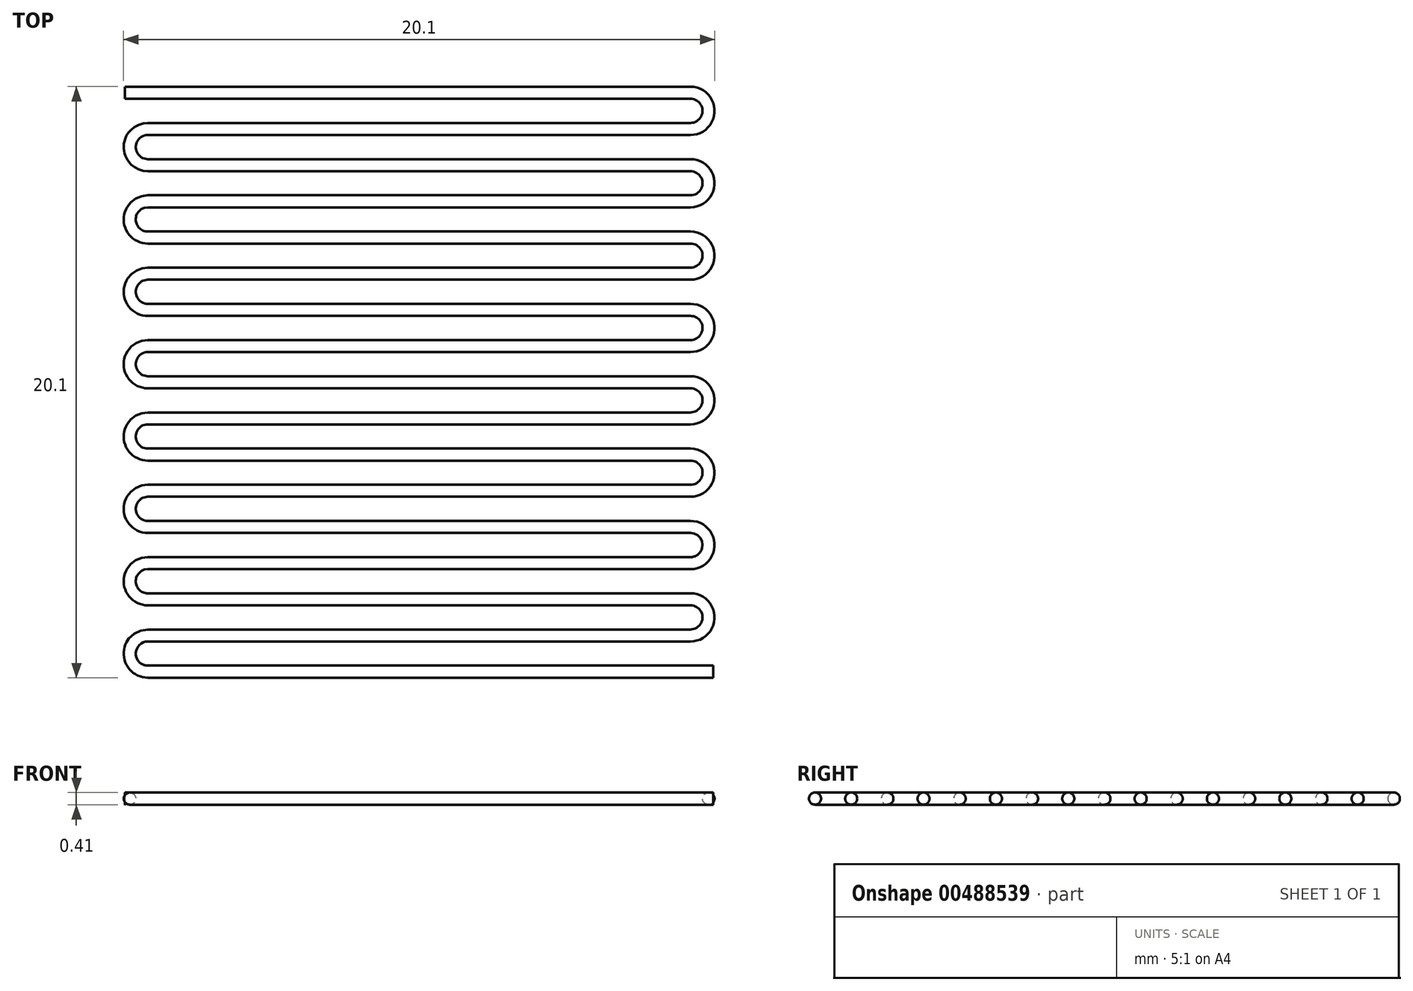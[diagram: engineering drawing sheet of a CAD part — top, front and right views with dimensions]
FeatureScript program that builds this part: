
annotation { "Feature Type Name" : "Feature", "Feature Type Description" : "" }
export const myFeature = defineFeature(function(context is Context, id is Id, definition is map)
    precondition{}
    {
        {
            assignVariable(context, id + "F0", {"name" : "d", "anyValue" : 0.4 * mm});
        }
        {
            var Q0;
            Q0=qCreatedBy(makeId("Top.planeOp"),FACE);
            cPlane(context, id + "F1", {"entities" : qUnion([Q0]), "cplaneType" : CPlaneType.OFFSET, "offset" : getVariable(context, 'd') / 2, "width" : 150 * mm, "height" : 150 * mm});
        }
        {
            var Q0;
            Q0=qCreatedBy(id+"F1.planeOp",FACE);
            var sketch = newSketch(context, id + "F2", { "sketchPlane" : qUnion([Q0])});
            skLineSegment(sketch, "E0.bottom", {"start": v(10, 10) * mm, "end": v(-10, 10) * mm});
            skLineSegment(sketch, "E0.top", {"start": v(10, -10) * mm, "end": v(-10, -10) * mm});
            skLineSegment(sketch, "E0.left", {"start": v(10, 10) * mm, "end": v(10, -10) * mm});
            skLineSegment(sketch, "E0.right", {"start": v(-10, 10) * mm, "end": v(-10, -10) * mm});
            skPoint(sketch, "E0.middle", {"position": v(0, 0) * mm});
            skLineSegment(sketch, "E1", {"start": v(-9.84, 10) * mm, "end": v(-8.61, 10) * mm});
            skLineSegment(sketch, "E2", {"start": v(-8.61, 10) * mm, "end": v(-7.38, 10) * mm});
            skLineSegment(sketch, "E3", {"start": v(-7.38, 10) * mm, "end": v(-6.15, 10) * mm});
            skLineSegment(sketch, "E4", {"start": v(-6.15, 10) * mm, "end": v(-4.92, 10) * mm});
            skLineSegment(sketch, "E5", {"start": v(-4.92, 10) * mm, "end": v(-3.7, 10) * mm});
            skLineSegment(sketch, "E6", {"start": v(-3.7, 10) * mm, "end": v(-2.46, 10) * mm});
            skLineSegment(sketch, "E7", {"start": v(-2.46, 10) * mm, "end": v(-1.23, 10) * mm});
            skLineSegment(sketch, "E8", {"start": v(-1.23, 10) * mm, "end": v(0, 10) * mm});
            skLineSegment(sketch, "E9", {"start": v(0, 10) * mm, "end": v(1.23, 10) * mm});
            skLineSegment(sketch, "E10", {"start": v(1.23, 10) * mm, "end": v(2.46, 10) * mm});
            skLineSegment(sketch, "E11", {"start": v(2.46, 10) * mm, "end": v(3.69, 10) * mm});
            skLineSegment(sketch, "E12", {"start": v(3.69, 10) * mm, "end": v(4.92, 10) * mm});
            skLineSegment(sketch, "E13", {"start": v(4.92, 10) * mm, "end": v(6.15, 10) * mm});
            skLineSegment(sketch, "E14", {"start": v(6.15, 10) * mm, "end": v(7.38, 10) * mm});
            skLineSegment(sketch, "E15", {"start": v(7.38, 10) * mm, "end": v(8.6, 10) * mm});
            skLineSegment(sketch, "E16", {"start": v(8.6, 10) * mm, "end": v(9.84, 10) * mm});
            skLineSegment(sketch, "E17", {"start": v(-9.84, 10) * mm, "end": v(-9.84, -10) * mm});
            skLineSegment(sketch, "E18", {"start": v(-8.61, 10) * mm, "end": v(-8.6, -10) * mm});
            skLineSegment(sketch, "E19", {"start": v(-8.6, -10) * mm, "end": v(-9.84, -10) * mm});
            skLineSegment(sketch, "E20", {"start": v(-7.38, 10) * mm, "end": v(-7.38, -10) * mm});
            skLineSegment(sketch, "E21", {"start": v(-7.38, -10) * mm, "end": v(-8.6, -10) * mm});
            skLineSegment(sketch, "E22", {"start": v(-6.15, 10) * mm, "end": v(-6.15, -10) * mm});
            skLineSegment(sketch, "E23", {"start": v(-6.15, -10) * mm, "end": v(-7.38, -10) * mm});
            skLineSegment(sketch, "E24", {"start": v(-4.92, 10) * mm, "end": v(-4.92, -10) * mm});
            skLineSegment(sketch, "E25", {"start": v(-4.92, -10) * mm, "end": v(-6.15, -10) * mm});
            skLineSegment(sketch, "E26", {"start": v(-3.7, 10) * mm, "end": v(-3.69, -10) * mm});
            skLineSegment(sketch, "E27", {"start": v(-3.69, -10) * mm, "end": v(-4.92, -10) * mm});
            skLineSegment(sketch, "E28", {"start": v(-2.46, 10) * mm, "end": v(-2.46, -10) * mm});
            skLineSegment(sketch, "E29", {"start": v(-2.46, -10) * mm, "end": v(-3.69, -10) * mm});
            skLineSegment(sketch, "E30", {"start": v(-1.23, 10) * mm, "end": v(-1.23, -10) * mm});
            skLineSegment(sketch, "E31", {"start": v(-1.23, -10) * mm, "end": v(-2.46, -10) * mm});
            skLineSegment(sketch, "E32", {"start": v(0, 10) * mm, "end": v(0, -10) * mm});
            skLineSegment(sketch, "E33", {"start": v(0, -10) * mm, "end": v(-1.23, -10) * mm});
            skLineSegment(sketch, "E34", {"start": v(1.23, 10) * mm, "end": v(1.23, -10) * mm});
            skLineSegment(sketch, "E35", {"start": v(1.23, -10) * mm, "end": v(0, -10) * mm});
            skLineSegment(sketch, "E36", {"start": v(2.46, 10) * mm, "end": v(2.46, -10) * mm});
            skLineSegment(sketch, "E37", {"start": v(2.46, -10) * mm, "end": v(1.23, -10) * mm});
            skLineSegment(sketch, "E38", {"start": v(3.69, 10) * mm, "end": v(3.69, -10) * mm});
            skLineSegment(sketch, "E39", {"start": v(3.69, -10) * mm, "end": v(2.46, -10) * mm});
            skLineSegment(sketch, "E40", {"start": v(4.92, 10) * mm, "end": v(4.92, -10) * mm});
            skLineSegment(sketch, "E41", {"start": v(4.92, -10) * mm, "end": v(3.69, -10) * mm});
            skLineSegment(sketch, "E42", {"start": v(6.15, 10) * mm, "end": v(6.15, -10) * mm});
            skLineSegment(sketch, "E43", {"start": v(6.15, -10) * mm, "end": v(4.92, -10) * mm});
            skLineSegment(sketch, "E44", {"start": v(7.38, 10) * mm, "end": v(7.38, -10) * mm});
            skLineSegment(sketch, "E45", {"start": v(7.38, -10) * mm, "end": v(6.15, -10) * mm});
            skLineSegment(sketch, "E46", {"start": v(8.6, 10) * mm, "end": v(8.6, -10) * mm});
            skLineSegment(sketch, "E47", {"start": v(8.6, -10) * mm, "end": v(7.38, -10) * mm});
            skLineSegment(sketch, "E48", {"start": v(9.84, 10) * mm, "end": v(9.84, -10) * mm});
            skLineSegment(sketch, "E49", {"start": v(9.84, -10) * mm, "end": v(8.6, -10) * mm});
            skLineSegment(sketch, "E50", {"start": v(-10, 10) * mm, "end": v(-10, 9.84) * mm});
            skLineSegment(sketch, "E51", {"start": v(-10, -10) * mm, "end": v(-10, -9.84) * mm});
            skLineSegment(sketch, "E52", {"start": v(-10, 9.84) * mm, "end": v(-10, 9.23) * mm});
            skLineSegment(sketch, "E53", {"start": v(-9.84, 9.23) * mm, "end": v(-8.6, 9.23) * mm});
            skLineSegment(sketch, "E54", {"start": v(-8.6, 9.23) * mm, "end": v(-7.38, 9.23) * mm});
            skLineSegment(sketch, "E55", {"start": v(-7.38, 9.23) * mm, "end": v(-6.15, 9.23) * mm});
            skLineSegment(sketch, "E56", {"start": v(-6.15, 9.23) * mm, "end": v(-4.92, 9.23) * mm});
            skLineSegment(sketch, "E57", {"start": v(-4.92, 9.23) * mm, "end": v(-3.7, 9.23) * mm});
            skLineSegment(sketch, "E58", {"start": v(-3.7, 9.23) * mm, "end": v(-2.46, 9.23) * mm});
            skLineSegment(sketch, "E59", {"start": v(-2.46, 9.23) * mm, "end": v(-1.23, 9.23) * mm});
            skLineSegment(sketch, "E60", {"start": v(-1.23, 9.23) * mm, "end": v(0, 9.23) * mm});
            skLineSegment(sketch, "E61", {"start": v(0, 9.23) * mm, "end": v(1.23, 9.23) * mm});
            skLineSegment(sketch, "E62", {"start": v(1.23, 9.23) * mm, "end": v(2.46, 9.23) * mm});
            skLineSegment(sketch, "E63", {"start": v(2.46, 9.23) * mm, "end": v(3.69, 9.23) * mm});
            skLineSegment(sketch, "E64", {"start": v(3.69, 9.23) * mm, "end": v(4.92, 9.23) * mm});
            skLineSegment(sketch, "E65", {"start": v(4.92, 9.23) * mm, "end": v(6.15, 9.23) * mm});
            skLineSegment(sketch, "E66", {"start": v(6.15, 9.23) * mm, "end": v(7.38, 9.23) * mm});
            skLineSegment(sketch, "E67", {"start": v(7.38, 9.23) * mm, "end": v(8.6, 9.23) * mm});
            skLineSegment(sketch, "E68", {"start": v(8.6, 9.23) * mm, "end": v(9.84, 9.23) * mm});
            skLineSegment(sketch, "E69", {"start": v(-10, -9.84) * mm, "end": v(-10, -9.22) * mm});
            skLineSegment(sketch, "E70", {"start": v(-9.84, -9.22) * mm, "end": v(-8.6, -9.22) * mm});
            skLineSegment(sketch, "E71", {"start": v(-8.6, -9.22) * mm, "end": v(-7.38, -9.22) * mm});
            skLineSegment(sketch, "E72", {"start": v(-7.38, -9.22) * mm, "end": v(-6.15, -9.22) * mm});
            skLineSegment(sketch, "E73", {"start": v(-6.15, -9.22) * mm, "end": v(-4.92, -9.22) * mm});
            skLineSegment(sketch, "E74", {"start": v(-4.92, -9.22) * mm, "end": v(-3.69, -9.22) * mm});
            skLineSegment(sketch, "E75", {"start": v(-3.69, -9.22) * mm, "end": v(-2.46, -9.22) * mm});
            skLineSegment(sketch, "E76", {"start": v(-2.46, -9.22) * mm, "end": v(-1.23, -9.22) * mm});
            skLineSegment(sketch, "E77", {"start": v(-1.23, -9.22) * mm, "end": v(0, -9.22) * mm});
            skLineSegment(sketch, "E78", {"start": v(0, -9.22) * mm, "end": v(1.23, -9.22) * mm});
            skLineSegment(sketch, "E79", {"start": v(1.23, -9.22) * mm, "end": v(2.46, -9.22) * mm});
            skLineSegment(sketch, "E80", {"start": v(2.46, -9.22) * mm, "end": v(3.69, -9.22) * mm});
            skLineSegment(sketch, "E81", {"start": v(3.69, -9.22) * mm, "end": v(4.92, -9.22) * mm});
            skLineSegment(sketch, "E82", {"start": v(4.92, -9.22) * mm, "end": v(6.15, -9.22) * mm});
            skLineSegment(sketch, "E83", {"start": v(6.15, -9.22) * mm, "end": v(7.38, -9.22) * mm});
            skLineSegment(sketch, "E84", {"start": v(7.38, -9.22) * mm, "end": v(8.6, -9.22) * mm});
            skLineSegment(sketch, "E85", {"start": v(8.6, -9.22) * mm, "end": v(9.84, -9.22) * mm});
            skLineSegment(sketch, "E86", {"start": v(-9.84, -9.22) * mm, "end": v(-9.84, 9.23) * mm});
            skLineSegment(sketch, "E87", {"start": v(-8.61, 9.23) * mm, "end": v(-8.6, -9.22) * mm});
            skLineSegment(sketch, "E88", {"start": v(-7.38, -9.22) * mm, "end": v(-7.38, 9.23) * mm});
            skLineSegment(sketch, "E89", {"start": v(-6.15, 9.23) * mm, "end": v(-6.15, -9.22) * mm});
            skLineSegment(sketch, "E90", {"start": v(-4.92, -9.22) * mm, "end": v(-4.92, 9.23) * mm});
            skLineSegment(sketch, "E91", {"start": v(-3.7, 9.23) * mm, "end": v(-3.69, -9.22) * mm});
            skLineSegment(sketch, "E92", {"start": v(-2.46, -9.22) * mm, "end": v(-2.46, 9.23) * mm});
            skLineSegment(sketch, "E93", {"start": v(-1.23, 9.23) * mm, "end": v(-1.23, -9.22) * mm});
            skLineSegment(sketch, "E94", {"start": v(0, -9.22) * mm, "end": v(0, 9.23) * mm});
            skLineSegment(sketch, "E95", {"start": v(1.23, 9.23) * mm, "end": v(1.23, -9.22) * mm});
            skLineSegment(sketch, "E96", {"start": v(2.46, -9.22) * mm, "end": v(2.46, 9.23) * mm});
            skLineSegment(sketch, "E97", {"start": v(3.69, 9.23) * mm, "end": v(3.69, -9.22) * mm});
            skLineSegment(sketch, "E98", {"start": v(4.92, -9.22) * mm, "end": v(4.92, 9.23) * mm});
            skLineSegment(sketch, "E99", {"start": v(6.15, -9.22) * mm, "end": v(6.15, 9.23) * mm});
            skLineSegment(sketch, "E100", {"start": v(7.38, 9.23) * mm, "end": v(7.38, -9.22) * mm});
            skLineSegment(sketch, "E101", {"start": v(8.6, -9.22) * mm, "end": v(8.6, 9.23) * mm});
            skLineSegment(sketch, "E102", {"start": v(9.84, 9.23) * mm, "end": v(9.84, -9.22) * mm});
            skArc(sketch, "E103", {"start": v(9.84, 9.23) * mm, "mid": v(9.22, 9.84) * mm, "end": v(8.6, 9.23) * mm});
            skArc(sketch, "E104", {"start": v(7.38, 9.23) * mm, "mid": v(6.76, 9.84) * mm, "end": v(6.15, 9.23) * mm});
            skArc(sketch, "E105", {"start": v(4.92, 9.23) * mm, "mid": v(4.3, 9.84) * mm, "end": v(3.69, 9.23) * mm});
            skArc(sketch, "E106", {"start": v(2.46, 9.23) * mm, "mid": v(1.84, 9.84) * mm, "end": v(1.23, 9.23) * mm});
            skArc(sketch, "E107", {"start": v(0, 9.23) * mm, "mid": v(-0.62, 9.84) * mm, "end": v(-1.23, 9.23) * mm});
            skArc(sketch, "E108", {"start": v(-2.46, 9.23) * mm, "mid": v(-3.07, 9.84) * mm, "end": v(-3.69, 9.23) * mm});
            skArc(sketch, "E109", {"start": v(-4.92, 9.23) * mm, "mid": v(-5.54, 9.84) * mm, "end": v(-6.15, 9.23) * mm});
            skArc(sketch, "E110", {"start": v(-7.38, 9.23) * mm, "mid": v(-8, 9.84) * mm, "end": v(-8.6, 9.23) * mm});
            skArc(sketch, "E111", {"start": v(4.92, -9.22) * mm, "mid": v(5.53, -9.84) * mm, "end": v(6.15, -9.22) * mm});
            skArc(sketch, "E112", {"start": v(2.46, -9.22) * mm, "mid": v(3.07, -9.84) * mm, "end": v(3.69, -9.22) * mm});
            skArc(sketch, "E113", {"start": v(0, -9.22) * mm, "mid": v(0.62, -9.84) * mm, "end": v(1.23, -9.22) * mm});
            skArc(sketch, "E114", {"start": v(-2.46, -9.22) * mm, "mid": v(-1.85, -9.84) * mm, "end": v(-1.23, -9.22) * mm});
            skArc(sketch, "E115", {"start": v(-4.92, -9.22) * mm, "mid": v(-4.3, -9.84) * mm, "end": v(-3.69, -9.22) * mm});
            skArc(sketch, "E116", {"start": v(-9.84, -9.22) * mm, "mid": v(-9.22, -9.84) * mm, "end": v(-8.6, -9.22) * mm});
            skArc(sketch, "E117", {"start": v(7.38, -9.22) * mm, "mid": v(8, -9.84) * mm, "end": v(8.6, -9.22) * mm});
            skArc(sketch, "E118", {"start": v(-7.38, -9.22) * mm, "mid": v(-6.77, -9.84) * mm, "end": v(-6.15, -9.22) * mm});
            skLineSegment(sketch, "E119", {"start": v(-10, 10) * mm, "end": v(-9.84, 10) * mm});
            skLineSegment(sketch, "E120", {"start": v(9.84, 10) * mm, "end": v(10, 10) * mm});
            skLineSegment(sketch, "E121", {"start": v(-10, 9.84) * mm, "end": v(10, 9.84) * mm});
            skLineSegment(sketch, "E122", {"start": v(-10, -9.84) * mm, "end": v(10, -9.84) * mm});
            skLineSegment(sketch, "E123", {"start": v(9.84, -10) * mm, "end": v(9.84, 9.23) * mm});
            skLineSegment(sketch, "E124", {"start": v(-9.84, -9.22) * mm, "end": v(-9.84, 10) * mm});
            skSolve(sketch);
        }
        {
            var Q0;
            Q0=sQuery(id+"F2.wireOp",EDGE,"E123");
            var Q1;
            Q1=sQuery(id+"F2.wireOp",VERTEX,"E123.start");
            cPlane(context, id + "F3", {"entities" : qUnion([Q0, Q1]), "cplaneType" : CPlaneType.LINE_POINT, "offset" : 25 * mm, "width" : 150 * mm, "height" : 150 * mm});
        }
        {
            var Q0;
            Q0=qCreatedBy(id+"F3.planeOp",FACE);
            var sketch = newSketch(context, id + "F4", { "sketchPlane" : qUnion([Q0])});
            skCircle(sketch, "E125", {"center": v(-9.84, 0.2) * mm, "radius": 0.2 * mm});
            skSolve(sketch);
        }
        {
            var Q0;
            Q0=qCreatedBy(id+"F1.planeOp",FACE);
            cPlane(context, id + "F5", {"entities" : qUnion([Q0]), "cplaneType" : CPlaneType.OFFSET, "offset" : getVariable(context, 'd'), "width" : 150 * mm, "height" : 150 * mm});
        }
        {
            var Q0;
            Q0=qCreatedBy(id+"F5.planeOp",FACE);
            var sketch = newSketch(context, id + "F6", { "sketchPlane" : qUnion([Q0])});
            skLineSegment(sketch, "E126.bottom", {"start": v(-30, 10) * mm, "end": v(-30, -10) * mm});
            skLineSegment(sketch, "E126.top", {"start": v(-10, 10) * mm, "end": v(-10, -10) * mm});
            skLineSegment(sketch, "E126.left", {"start": v(-30, 10) * mm, "end": v(-10, 10) * mm});
            skLineSegment(sketch, "E126.right", {"start": v(-30, -10) * mm, "end": v(-10, -10) * mm});
            skPoint(sketch, "E126.middle", {"position": v(-20, 0) * mm});
            skLineSegment(sketch, "E127", {"start": v(-30, -9.84) * mm, "end": v(-30, -8.6) * mm});
            skLineSegment(sketch, "E128", {"start": v(-30, -8.6) * mm, "end": v(-30, -7.38) * mm});
            skLineSegment(sketch, "E129", {"start": v(-30, -7.38) * mm, "end": v(-30, -6.15) * mm});
            skLineSegment(sketch, "E130", {"start": v(-30, -6.15) * mm, "end": v(-30, -4.92) * mm});
            skLineSegment(sketch, "E131", {"start": v(-30, -4.92) * mm, "end": v(-30, -3.69) * mm});
            skLineSegment(sketch, "E132", {"start": v(-30, -3.69) * mm, "end": v(-30, -2.46) * mm});
            skLineSegment(sketch, "E133", {"start": v(-30, -2.46) * mm, "end": v(-30, -1.23) * mm});
            skLineSegment(sketch, "E134", {"start": v(-30, -1.23) * mm, "end": v(-30, 0) * mm});
            skLineSegment(sketch, "E135", {"start": v(-30, 0) * mm, "end": v(-30, 1.23) * mm});
            skLineSegment(sketch, "E136", {"start": v(-30, 1.23) * mm, "end": v(-30, 2.46) * mm});
            skLineSegment(sketch, "E137", {"start": v(-30, 2.46) * mm, "end": v(-30, 3.69) * mm});
            skLineSegment(sketch, "E138", {"start": v(-30, 3.69) * mm, "end": v(-30, 4.92) * mm});
            skLineSegment(sketch, "E139", {"start": v(-30, 4.92) * mm, "end": v(-30, 6.15) * mm});
            skLineSegment(sketch, "E140", {"start": v(-30, 6.15) * mm, "end": v(-30, 7.38) * mm});
            skLineSegment(sketch, "E141", {"start": v(-30, 7.38) * mm, "end": v(-30, 8.6) * mm});
            skLineSegment(sketch, "E142", {"start": v(-30, 8.6) * mm, "end": v(-30, 9.84) * mm});
            skLineSegment(sketch, "E143", {"start": v(-30, -9.84) * mm, "end": v(-10, -9.84) * mm});
            skLineSegment(sketch, "E144", {"start": v(-30, -8.6) * mm, "end": v(-10, -8.6) * mm});
            skLineSegment(sketch, "E145", {"start": v(-10, -8.6) * mm, "end": v(-10, -9.84) * mm});
            skLineSegment(sketch, "E146", {"start": v(-30, -7.38) * mm, "end": v(-10, -7.38) * mm});
            skLineSegment(sketch, "E147", {"start": v(-10, -7.38) * mm, "end": v(-10, -8.6) * mm});
            skLineSegment(sketch, "E148", {"start": v(-30, -6.15) * mm, "end": v(-10, -6.15) * mm});
            skLineSegment(sketch, "E149", {"start": v(-10, -6.15) * mm, "end": v(-10, -7.38) * mm});
            skLineSegment(sketch, "E150", {"start": v(-30, -4.92) * mm, "end": v(-10, -4.92) * mm});
            skLineSegment(sketch, "E151", {"start": v(-10, -4.92) * mm, "end": v(-10, -6.15) * mm});
            skLineSegment(sketch, "E152", {"start": v(-30, -3.69) * mm, "end": v(-10, -3.69) * mm});
            skLineSegment(sketch, "E153", {"start": v(-10, -3.69) * mm, "end": v(-10, -4.92) * mm});
            skLineSegment(sketch, "E154", {"start": v(-30, -2.46) * mm, "end": v(-10, -2.46) * mm});
            skLineSegment(sketch, "E155", {"start": v(-10, -2.46) * mm, "end": v(-10, -3.69) * mm});
            skLineSegment(sketch, "E156", {"start": v(-30, -1.23) * mm, "end": v(-10, -1.23) * mm});
            skLineSegment(sketch, "E157", {"start": v(-10, -1.23) * mm, "end": v(-10, -2.46) * mm});
            skLineSegment(sketch, "E158", {"start": v(-30, 0) * mm, "end": v(-10, 0) * mm});
            skLineSegment(sketch, "E159", {"start": v(-10, 0) * mm, "end": v(-10, -1.23) * mm});
            skLineSegment(sketch, "E160", {"start": v(-30, 1.23) * mm, "end": v(-10, 1.23) * mm});
            skLineSegment(sketch, "E161", {"start": v(-10, 1.23) * mm, "end": v(-10, 0) * mm});
            skLineSegment(sketch, "E162", {"start": v(-30, 2.46) * mm, "end": v(-10, 2.46) * mm});
            skLineSegment(sketch, "E163", {"start": v(-10, 2.46) * mm, "end": v(-10, 1.23) * mm});
            skLineSegment(sketch, "E164", {"start": v(-30, 3.7) * mm, "end": v(-10, 3.7) * mm});
            skLineSegment(sketch, "E165", {"start": v(-10, 3.7) * mm, "end": v(-10, 2.46) * mm});
            skLineSegment(sketch, "E166", {"start": v(-30, 4.92) * mm, "end": v(-10, 4.92) * mm});
            skLineSegment(sketch, "E167", {"start": v(-10, 4.92) * mm, "end": v(-10, 3.7) * mm});
            skLineSegment(sketch, "E168", {"start": v(-30, 6.15) * mm, "end": v(-10, 6.15) * mm});
            skLineSegment(sketch, "E169", {"start": v(-10, 6.15) * mm, "end": v(-10, 4.92) * mm});
            skLineSegment(sketch, "E170", {"start": v(-30, 7.38) * mm, "end": v(-10, 7.38) * mm});
            skLineSegment(sketch, "E171", {"start": v(-10, 7.38) * mm, "end": v(-10, 6.15) * mm});
            skLineSegment(sketch, "E172", {"start": v(-30, 8.6) * mm, "end": v(-10, 8.6) * mm});
            skLineSegment(sketch, "E173", {"start": v(-10, 8.6) * mm, "end": v(-10, 7.38) * mm});
            skLineSegment(sketch, "E174", {"start": v(-30, 9.84) * mm, "end": v(-10, 9.84) * mm});
            skLineSegment(sketch, "E175", {"start": v(-10, 9.84) * mm, "end": v(-10, 8.6) * mm});
            skLineSegment(sketch, "E176", {"start": v(-30, -10) * mm, "end": v(-29.84, -10) * mm});
            skLineSegment(sketch, "E177", {"start": v(-10, -10) * mm, "end": v(-10.16, -10) * mm});
            skLineSegment(sketch, "E178", {"start": v(-29.84, -10) * mm, "end": v(-29.23, -10) * mm});
            skLineSegment(sketch, "E179", {"start": v(-29.23, -9.84) * mm, "end": v(-29.23, -8.6) * mm});
            skLineSegment(sketch, "E180", {"start": v(-29.23, -8.6) * mm, "end": v(-29.23, -7.38) * mm});
            skLineSegment(sketch, "E181", {"start": v(-29.23, -7.38) * mm, "end": v(-29.23, -6.15) * mm});
            skLineSegment(sketch, "E182", {"start": v(-29.23, -6.15) * mm, "end": v(-29.23, -4.92) * mm});
            skLineSegment(sketch, "E183", {"start": v(-29.23, -4.92) * mm, "end": v(-29.23, -3.69) * mm});
            skLineSegment(sketch, "E184", {"start": v(-29.23, -3.69) * mm, "end": v(-29.23, -2.46) * mm});
            skLineSegment(sketch, "E185", {"start": v(-29.23, -2.46) * mm, "end": v(-29.23, -1.23) * mm});
            skLineSegment(sketch, "E186", {"start": v(-29.23, -1.23) * mm, "end": v(-29.23, 0) * mm});
            skLineSegment(sketch, "E187", {"start": v(-29.23, 0) * mm, "end": v(-29.23, 1.23) * mm});
            skLineSegment(sketch, "E188", {"start": v(-29.23, 1.23) * mm, "end": v(-29.23, 2.46) * mm});
            skLineSegment(sketch, "E189", {"start": v(-29.23, 2.46) * mm, "end": v(-29.23, 3.69) * mm});
            skLineSegment(sketch, "E190", {"start": v(-29.23, 3.69) * mm, "end": v(-29.23, 4.92) * mm});
            skLineSegment(sketch, "E191", {"start": v(-29.23, 4.92) * mm, "end": v(-29.23, 6.15) * mm});
            skLineSegment(sketch, "E192", {"start": v(-29.23, 6.15) * mm, "end": v(-29.23, 7.38) * mm});
            skLineSegment(sketch, "E193", {"start": v(-29.23, 7.38) * mm, "end": v(-29.23, 8.6) * mm});
            skLineSegment(sketch, "E194", {"start": v(-29.23, 8.6) * mm, "end": v(-29.23, 9.84) * mm});
            skLineSegment(sketch, "E195", {"start": v(-10.16, -10) * mm, "end": v(-10.78, -10) * mm});
            skLineSegment(sketch, "E196", {"start": v(-10.78, -9.84) * mm, "end": v(-10.78, -8.6) * mm});
            skLineSegment(sketch, "E197", {"start": v(-10.78, -8.6) * mm, "end": v(-10.78, -7.38) * mm});
            skLineSegment(sketch, "E198", {"start": v(-10.78, -7.38) * mm, "end": v(-10.78, -6.15) * mm});
            skLineSegment(sketch, "E199", {"start": v(-10.78, -6.15) * mm, "end": v(-10.78, -4.92) * mm});
            skLineSegment(sketch, "E200", {"start": v(-10.78, -4.92) * mm, "end": v(-10.78, -3.69) * mm});
            skLineSegment(sketch, "E201", {"start": v(-10.78, -3.69) * mm, "end": v(-10.78, -2.46) * mm});
            skLineSegment(sketch, "E202", {"start": v(-10.78, -2.46) * mm, "end": v(-10.78, -1.23) * mm});
            skLineSegment(sketch, "E203", {"start": v(-10.78, -1.23) * mm, "end": v(-10.78, 0) * mm});
            skLineSegment(sketch, "E204", {"start": v(-10.78, 0) * mm, "end": v(-10.78, 1.23) * mm});
            skLineSegment(sketch, "E205", {"start": v(-10.78, 1.23) * mm, "end": v(-10.78, 2.46) * mm});
            skLineSegment(sketch, "E206", {"start": v(-10.78, 2.46) * mm, "end": v(-10.78, 3.7) * mm});
            skLineSegment(sketch, "E207", {"start": v(-10.78, 3.7) * mm, "end": v(-10.78, 4.92) * mm});
            skLineSegment(sketch, "E208", {"start": v(-10.78, 4.92) * mm, "end": v(-10.78, 6.15) * mm});
            skLineSegment(sketch, "E209", {"start": v(-10.78, 6.15) * mm, "end": v(-10.78, 7.38) * mm});
            skLineSegment(sketch, "E210", {"start": v(-10.78, 7.38) * mm, "end": v(-10.78, 8.6) * mm});
            skLineSegment(sketch, "E211", {"start": v(-10.78, 8.6) * mm, "end": v(-10.78, 9.84) * mm});
            skLineSegment(sketch, "E212", {"start": v(-10.78, -9.84) * mm, "end": v(-29.23, -9.84) * mm});
            skLineSegment(sketch, "E213", {"start": v(-29.23, -8.6) * mm, "end": v(-10.78, -8.6) * mm});
            skLineSegment(sketch, "E214", {"start": v(-10.78, -7.38) * mm, "end": v(-29.23, -7.38) * mm});
            skLineSegment(sketch, "E215", {"start": v(-29.23, -6.15) * mm, "end": v(-10.78, -6.15) * mm});
            skLineSegment(sketch, "E216", {"start": v(-10.78, -4.92) * mm, "end": v(-29.23, -4.92) * mm});
            skLineSegment(sketch, "E217", {"start": v(-29.23, -3.69) * mm, "end": v(-10.78, -3.69) * mm});
            skLineSegment(sketch, "E218", {"start": v(-10.78, -2.46) * mm, "end": v(-29.23, -2.46) * mm});
            skLineSegment(sketch, "E219", {"start": v(-29.23, -1.23) * mm, "end": v(-10.78, -1.23) * mm});
            skLineSegment(sketch, "E220", {"start": v(-10.78, 0) * mm, "end": v(-29.23, 0) * mm});
            skLineSegment(sketch, "E221", {"start": v(-29.23, 1.23) * mm, "end": v(-10.78, 1.23) * mm});
            skLineSegment(sketch, "E222", {"start": v(-10.78, 2.46) * mm, "end": v(-29.23, 2.46) * mm});
            skLineSegment(sketch, "E223", {"start": v(-29.23, 3.7) * mm, "end": v(-10.78, 3.7) * mm});
            skLineSegment(sketch, "E224", {"start": v(-10.78, 4.92) * mm, "end": v(-29.23, 4.92) * mm});
            skLineSegment(sketch, "E225", {"start": v(-10.78, 6.15) * mm, "end": v(-29.23, 6.15) * mm});
            skLineSegment(sketch, "E226", {"start": v(-29.23, 7.38) * mm, "end": v(-10.78, 7.38) * mm});
            skLineSegment(sketch, "E227", {"start": v(-10.78, 8.6) * mm, "end": v(-29.23, 8.6) * mm});
            skLineSegment(sketch, "E228", {"start": v(-29.23, 9.84) * mm, "end": v(-10.78, 9.84) * mm});
            skArc(sketch, "E229", {"start": v(-29.23, 9.84) * mm, "mid": v(-29.84, 9.22) * mm, "end": v(-29.23, 8.6) * mm});
            skArc(sketch, "E230", {"start": v(-29.23, 7.38) * mm, "mid": v(-29.84, 6.76) * mm, "end": v(-29.23, 6.15) * mm});
            skArc(sketch, "E231", {"start": v(-29.23, 4.92) * mm, "mid": v(-29.84, 4.3) * mm, "end": v(-29.23, 3.69) * mm});
            skArc(sketch, "E232", {"start": v(-29.23, 2.46) * mm, "mid": v(-29.84, 1.84) * mm, "end": v(-29.23, 1.23) * mm});
            skArc(sketch, "E233", {"start": v(-29.23, 0) * mm, "mid": v(-29.84, -0.61) * mm, "end": v(-29.23, -1.23) * mm});
            skArc(sketch, "E234", {"start": v(-29.23, -2.46) * mm, "mid": v(-29.84, -3.07) * mm, "end": v(-29.23, -3.69) * mm});
            skArc(sketch, "E235", {"start": v(-29.23, -4.92) * mm, "mid": v(-29.84, -5.53) * mm, "end": v(-29.23, -6.15) * mm});
            skArc(sketch, "E236", {"start": v(-29.23, -7.38) * mm, "mid": v(-29.84, -8) * mm, "end": v(-29.23, -8.6) * mm});
            skArc(sketch, "E237", {"start": v(-10.78, 4.92) * mm, "mid": v(-10.16, 5.53) * mm, "end": v(-10.78, 6.15) * mm});
            skArc(sketch, "E238", {"start": v(-10.78, 2.46) * mm, "mid": v(-10.16, 3.08) * mm, "end": v(-10.78, 3.7) * mm});
            skArc(sketch, "E239", {"start": v(-10.78, 0) * mm, "mid": v(-10.16, 0.62) * mm, "end": v(-10.78, 1.23) * mm});
            skArc(sketch, "E240", {"start": v(-10.78, -2.46) * mm, "mid": v(-10.16, -1.84) * mm, "end": v(-10.78, -1.23) * mm});
            skArc(sketch, "E241", {"start": v(-10.78, -4.92) * mm, "mid": v(-10.16, -4.3) * mm, "end": v(-10.78, -3.69) * mm});
            skArc(sketch, "E242", {"start": v(-10.78, -9.84) * mm, "mid": v(-10.16, -9.22) * mm, "end": v(-10.78, -8.6) * mm});
            skArc(sketch, "E243", {"start": v(-10.78, 7.38) * mm, "mid": v(-10.16, 8) * mm, "end": v(-10.78, 8.6) * mm});
            skArc(sketch, "E244", {"start": v(-10.78, -7.38) * mm, "mid": v(-10.16, -6.76) * mm, "end": v(-10.78, -6.15) * mm});
            skLineSegment(sketch, "E245", {"start": v(-30, -10) * mm, "end": v(-30, -9.84) * mm});
            skLineSegment(sketch, "E246", {"start": v(-30, 9.84) * mm, "end": v(-30, 10) * mm});
            skLineSegment(sketch, "E247", {"start": v(-29.84, -10) * mm, "end": v(-29.84, 10) * mm});
            skLineSegment(sketch, "E248", {"start": v(-10.16, -10) * mm, "end": v(-10.16, 10) * mm});
            skLineSegment(sketch, "E249", {"start": v(-10, 9.84) * mm, "end": v(-29.23, 9.84) * mm});
            skLineSegment(sketch, "E250.MirrorCS", {"start": v(-10, -10) * mm, "end": v(-9.84, -10) * mm});
            skLineSegment(sketch, "E251.MirrorCS", {"start": v(10, -10) * mm, "end": v(9.84, -10) * mm});
            skLineSegment(sketch, "E252.MirrorCS", {"start": v(10, -10) * mm, "end": v(10, -9.84) * mm});
            skLineSegment(sketch, "E253.MirrorCS", {"start": v(-9.84, -10) * mm, "end": v(-9.22, -10) * mm});
            skLineSegment(sketch, "E254.MirrorCS", {"start": v(10, 9.84) * mm, "end": v(10, 10) * mm});
            skLineSegment(sketch, "E255.MirrorCS", {"start": v(9.84, -10) * mm, "end": v(9.23, -10) * mm});
            skLineSegment(sketch, "E256.MirrorCS", {"start": v(9.23, -1.23) * mm, "end": v(9.23, 0) * mm});
            skLineSegment(sketch, "E257.MirrorCS", {"start": v(-9.22, 7.38) * mm, "end": v(-9.22, 8.6) * mm});
            skLineSegment(sketch, "E258.MirrorCS", {"start": v(9.23, 9.84) * mm, "end": v(-9.22, 9.84) * mm});
            skLineSegment(sketch, "E259.MirrorCS", {"start": v(-9.22, 0) * mm, "end": v(-9.22, 1.23) * mm});
            skLineSegment(sketch, "E260.MirrorCS", {"start": v(-9.22, 0) * mm, "end": v(9.23, 0) * mm});
            skLineSegment(sketch, "E261.MirrorCS", {"start": v(10, 7.38) * mm, "end": v(10, 8.6) * mm});
            skLineSegment(sketch, "E262.MirrorCS", {"start": v(9.23, 1.23) * mm, "end": v(-9.22, 1.23) * mm});
            skLineSegment(sketch, "E263.MirrorCS", {"start": v(9.23, -8.6) * mm, "end": v(9.23, -7.38) * mm});
            skLineSegment(sketch, "E264.MirrorCS", {"start": v(-9.22, -9.84) * mm, "end": v(-9.22, -8.6) * mm});
            skLineSegment(sketch, "E265.MirrorCS", {"start": v(10, 2.46) * mm, "end": v(10, 3.69) * mm});
            skLineSegment(sketch, "E266.MirrorCS", {"start": v(10, 6.15) * mm, "end": v(10, 7.38) * mm});
            skLineSegment(sketch, "E267.MirrorCS", {"start": v(9.23, 8.6) * mm, "end": v(9.22, 9.84) * mm});
            skLineSegment(sketch, "E268.MirrorCS", {"start": v(-9.22, 4.92) * mm, "end": v(9.23, 4.92) * mm});
            skLineSegment(sketch, "E269.MirrorCS", {"start": v(-9.22, 4.92) * mm, "end": v(-9.22, 6.15) * mm});
            skLineSegment(sketch, "E270.MirrorCS", {"start": v(9.23, 6.15) * mm, "end": v(9.23, 7.38) * mm});
            skLineSegment(sketch, "E271.MirrorCS", {"start": v(10, -8.6) * mm, "end": v(-10, -8.6) * mm});
            skLineSegment(sketch, "E272.MirrorCS", {"start": v(9.23, -6.15) * mm, "end": v(9.23, -4.92) * mm});
            skLineSegment(sketch, "E273.MirrorCS", {"start": v(10, -6.15) * mm, "end": v(-10, -6.15) * mm});
            skLineSegment(sketch, "E274.MirrorCS", {"start": v(10, 9.84) * mm, "end": v(-10, 9.84) * mm});
            skLineSegment(sketch, "E275.MirrorCS", {"start": v(-9.22, 6.15) * mm, "end": v(9.23, 6.15) * mm});
            skLineSegment(sketch, "E276.MirrorCS", {"start": v(9.23, -1.23) * mm, "end": v(-9.22, -1.23) * mm});
            skLineSegment(sketch, "E277.MirrorCS", {"start": v(10, 4.92) * mm, "end": v(10, 6.15) * mm});
            skLineSegment(sketch, "E278.MirrorCS", {"start": v(-9.22, -2.46) * mm, "end": v(-9.22, -1.23) * mm});
            skLineSegment(sketch, "E279.MirrorCS", {"start": v(10, 1.23) * mm, "end": v(10, 2.46) * mm});
            skLineSegment(sketch, "E280.MirrorCS", {"start": v(9.23, -3.69) * mm, "end": v(9.23, -2.46) * mm});
            skLineSegment(sketch, "E281.MirrorCS", {"start": v(-9.22, -4.92) * mm, "end": v(-9.22, -3.69) * mm});
            skLineSegment(sketch, "E282.MirrorCS", {"start": v(10, -9.84) * mm, "end": v(-10, -9.84) * mm});
            skLineSegment(sketch, "E283.MirrorCS", {"start": v(9.23, 3.69) * mm, "end": v(9.23, 4.92) * mm});
            skLineSegment(sketch, "E284.MirrorCS", {"start": v(10, 3.69) * mm, "end": v(10, 4.92) * mm});
            skLineSegment(sketch, "E285.MirrorCS", {"start": v(9.23, 1.23) * mm, "end": v(9.23, 2.46) * mm});
            skLineSegment(sketch, "E286.MirrorCS", {"start": v(9.23, 3.7) * mm, "end": v(-9.22, 3.7) * mm});
            skLineSegment(sketch, "E287.MirrorCS", {"start": v(-9.22, 2.46) * mm, "end": v(9.22, 2.46) * mm});
            skLineSegment(sketch, "E288.MirrorCS", {"start": v(-9.22, 2.46) * mm, "end": v(-9.22, 3.7) * mm});
            skLineSegment(sketch, "E289.MirrorCS", {"start": v(10, 8.6) * mm, "end": v(10, 9.84) * mm});
            skLineSegment(sketch, "E290.MirrorCS", {"start": v(-9.22, -7.38) * mm, "end": v(-9.22, -6.15) * mm});
            skLineSegment(sketch, "E291.MirrorCS", {"start": v(10, -4.92) * mm, "end": v(-10, -4.92) * mm});
            skArc(sketch, "E292.MirrorCS", {"start": v(-9.22, -7.38) * mm, "mid": v(-9.84, -6.76) * mm, "end": v(-9.22, -6.15) * mm});
            skArc(sketch, "E293.MirrorCS", {"start": v(9.23, -7.38) * mm, "mid": v(9.84, -8) * mm, "end": v(9.23, -8.6) * mm});
            skLineSegment(sketch, "E294.MirrorCS", {"start": v(9.23, 2.46) * mm, "end": v(9.23, 3.69) * mm});
            skLineSegment(sketch, "E295.MirrorCS", {"start": v(-10, 9.84) * mm, "end": v(9.22, 9.84) * mm});
            skLineSegment(sketch, "E296.MirrorCS", {"start": v(10, 0) * mm, "end": v(10, 1.23) * mm});
            skLineSegment(sketch, "E297.MirrorCS", {"start": v(9.23, -3.69) * mm, "end": v(-9.22, -3.69) * mm});
            skArc(sketch, "E298.MirrorCS", {"start": v(9.23, 0) * mm, "mid": v(9.84, -0.61) * mm, "end": v(9.23, -1.23) * mm});
            skLineSegment(sketch, "E299.MirrorCS", {"start": v(9.23, -7.38) * mm, "end": v(9.23, -6.15) * mm});
            skLineSegment(sketch, "E300.MirrorCS", {"start": v(-9.22, -8.6) * mm, "end": v(-9.22, -7.38) * mm});
            skArc(sketch, "E301.MirrorCS", {"start": v(9.23, 4.92) * mm, "mid": v(9.84, 4.3) * mm, "end": v(9.23, 3.69) * mm});
            skLineSegment(sketch, "E302.MirrorCS", {"start": v(10, 3.7) * mm, "end": v(-10, 3.7) * mm});
            skArc(sketch, "E303.MirrorCS", {"start": v(-9.22, 4.92) * mm, "mid": v(-9.84, 5.53) * mm, "end": v(-9.22, 6.15) * mm});
            skLineSegment(sketch, "E304.MirrorCS", {"start": v(-9.22, 1.23) * mm, "end": v(-9.22, 2.46) * mm});
            skLineSegment(sketch, "E305.MirrorCS", {"start": v(10, -1.23) * mm, "end": v(10, 0) * mm});
            skLineSegment(sketch, "E306.MirrorCS", {"start": v(9.23, -9.84) * mm, "end": v(9.23, -8.6) * mm});
            skLineSegment(sketch, "E307.MirrorCS", {"start": v(10, -1.23) * mm, "end": v(-10, -1.23) * mm});
            skLineSegment(sketch, "E308.MirrorCS", {"start": v(9.23, -6.15) * mm, "end": v(-9.23, -6.15) * mm});
            skLineSegment(sketch, "E309.MirrorCS", {"start": v(-9.22, -3.69) * mm, "end": v(-9.22, -2.46) * mm});
            skLineSegment(sketch, "E310.MirrorCS", {"start": v(-9.22, -6.15) * mm, "end": v(-9.22, -4.92) * mm});
            skLineSegment(sketch, "E311.MirrorCS", {"start": v(9.84, -10) * mm, "end": v(9.84, 10) * mm});
            skLineSegment(sketch, "E312.MirrorCS", {"start": v(-9.22, -9.84) * mm, "end": v(9.22, -9.84) * mm});
            skArc(sketch, "E313.MirrorCS", {"start": v(-9.22, 2.46) * mm, "mid": v(-9.84, 3.08) * mm, "end": v(-9.22, 3.7) * mm});
            skArc(sketch, "E314.MirrorCS", {"start": v(-9.22, -4.92) * mm, "mid": v(-9.84, -4.3) * mm, "end": v(-9.22, -3.69) * mm});
            skLineSegment(sketch, "E315.MirrorCS", {"start": v(9.23, 7.38) * mm, "end": v(9.23, 8.6) * mm});
            skLineSegment(sketch, "E316.MirrorCS", {"start": v(9.23, -4.92) * mm, "end": v(9.23, -3.69) * mm});
            skLineSegment(sketch, "E317.MirrorCS", {"start": v(-9.22, 6.15) * mm, "end": v(-9.22, 7.38) * mm});
            skLineSegment(sketch, "E318.MirrorCS", {"start": v(-9.84, -10) * mm, "end": v(-9.84, 10) * mm});
            skLineSegment(sketch, "E319.MirrorCS", {"start": v(10, 6.15) * mm, "end": v(-10, 6.15) * mm});
            skArc(sketch, "E320.MirrorCS", {"start": v(9.23, 2.46) * mm, "mid": v(9.84, 1.84) * mm, "end": v(9.23, 1.23) * mm});
            skLineSegment(sketch, "E321.MirrorCS", {"start": v(10, -2.46) * mm, "end": v(10, -1.23) * mm});
            skLineSegment(sketch, "E322.MirrorCS", {"start": v(-9.22, -4.92) * mm, "end": v(9.22, -4.92) * mm});
            skLineSegment(sketch, "E323.MirrorCS", {"start": v(10, -3.69) * mm, "end": v(-10, -3.69) * mm});
            skLineSegment(sketch, "E324.MirrorCS", {"start": v(10, -3.69) * mm, "end": v(10, -2.46) * mm});
            skLineSegment(sketch, "E325.MirrorCS", {"start": v(10, -4.92) * mm, "end": v(10, -3.69) * mm});
            skLineSegment(sketch, "E326.MirrorCS", {"start": v(10, -7.38) * mm, "end": v(10, -6.15) * mm});
            skArc(sketch, "E327.MirrorCS", {"start": v(-9.22, 0) * mm, "mid": v(-9.84, 0.62) * mm, "end": v(-9.22, 1.23) * mm});
            skLineSegment(sketch, "E328.MirrorCS", {"start": v(-9.22, -7.38) * mm, "end": v(9.23, -7.38) * mm});
            skLineSegment(sketch, "E329.MirrorCS", {"start": v(10, -10) * mm, "end": v(-10, -10) * mm});
            skLineSegment(sketch, "E330.MirrorCS", {"start": v(10, 7.38) * mm, "end": v(-10, 7.38) * mm});
            skArc(sketch, "E331.MirrorCS", {"start": v(-9.22, 7.38) * mm, "mid": v(-9.84, 8) * mm, "end": v(-9.22, 8.6) * mm});
            skLineSegment(sketch, "E332.MirrorCS", {"start": v(10, 1.23) * mm, "end": v(-10, 1.23) * mm});
            skLineSegment(sketch, "E333.MirrorCS", {"start": v(9.23, -8.6) * mm, "end": v(-9.22, -8.6) * mm});
            skPoint(sketch, "E334.MirrorP", {"position": v(0, 0) * mm});
            skLineSegment(sketch, "E335.MirrorCS", {"start": v(10, 10) * mm, "end": v(-10, 10) * mm});
            skArc(sketch, "E336.MirrorCS", {"start": v(9.23, 7.38) * mm, "mid": v(9.84, 6.76) * mm, "end": v(9.23, 6.15) * mm});
            skLineSegment(sketch, "E337.MirrorCS", {"start": v(-9.22, -1.23) * mm, "end": v(-9.22, 0) * mm});
            skLineSegment(sketch, "E338.MirrorCS", {"start": v(9.23, -2.46) * mm, "end": v(9.23, -1.23) * mm});
            skLineSegment(sketch, "E339.MirrorCS", {"start": v(10, -2.46) * mm, "end": v(-10, -2.46) * mm});
            skLineSegment(sketch, "E340.MirrorCS", {"start": v(-9.22, -2.46) * mm, "end": v(9.23, -2.46) * mm});
            skLineSegment(sketch, "E341.MirrorCS", {"start": v(10, 10) * mm, "end": v(10, -10) * mm});
            skLineSegment(sketch, "E342.MirrorCS", {"start": v(10, -7.38) * mm, "end": v(-10, -7.38) * mm});
            skLineSegment(sketch, "E343.MirrorCS", {"start": v(10, -6.15) * mm, "end": v(10, -4.92) * mm});
            skArc(sketch, "E344.MirrorCS", {"start": v(9.22, 9.84) * mm, "mid": v(9.84, 9.23) * mm, "end": v(9.23, 8.6) * mm});
            skLineSegment(sketch, "E345.MirrorCS", {"start": v(9.23, 4.92) * mm, "end": v(9.23, 6.15) * mm});
            skLineSegment(sketch, "E346.MirrorCS", {"start": v(-9.22, 3.7) * mm, "end": v(-9.22, 4.92) * mm});
            skLineSegment(sketch, "E347.MirrorCS", {"start": v(-9.22, 8.6) * mm, "end": v(-9.23, 9.84) * mm});
            skArc(sketch, "E348.MirrorCS", {"start": v(9.23, -2.46) * mm, "mid": v(9.84, -3.07) * mm, "end": v(9.23, -3.69) * mm});
            skLineSegment(sketch, "E349.MirrorCS", {"start": v(10, 8.6) * mm, "end": v(-10, 8.6) * mm});
            skLineSegment(sketch, "E350.MirrorCS", {"start": v(-9.23, 8.6) * mm, "end": v(9.23, 8.6) * mm});
            skLineSegment(sketch, "E351.MirrorCS", {"start": v(10, 0) * mm, "end": v(-10, 0) * mm});
            skLineSegment(sketch, "E352.MirrorCS", {"start": v(10, -8.6) * mm, "end": v(10, -7.38) * mm});
            skArc(sketch, "E353.MirrorCS", {"start": v(-9.22, -9.84) * mm, "mid": v(-9.84, -9.22) * mm, "end": v(-9.22, -8.6) * mm});
            skArc(sketch, "E354.MirrorCS", {"start": v(-9.22, -2.46) * mm, "mid": v(-9.84, -1.84) * mm, "end": v(-9.22, -1.23) * mm});
            skLineSegment(sketch, "E355.MirrorCS", {"start": v(10, -9.84) * mm, "end": v(10, -8.6) * mm});
            skLineSegment(sketch, "E356.MirrorCS", {"start": v(9.22, 7.38) * mm, "end": v(-9.22, 7.38) * mm});
            skLineSegment(sketch, "E357.MirrorCS", {"start": v(10, 2.46) * mm, "end": v(-10, 2.46) * mm});
            skLineSegment(sketch, "E358.MirrorCS", {"start": v(9.23, 0) * mm, "end": v(9.23, 1.23) * mm});
            skArc(sketch, "E359.MirrorCS", {"start": v(9.22, -4.92) * mm, "mid": v(9.84, -5.53) * mm, "end": v(9.23, -6.15) * mm});
            skLineSegment(sketch, "E360.MirrorCS", {"start": v(10, 4.92) * mm, "end": v(-10, 4.92) * mm});
            skLineSegment(sketch, "E361", {"start": v(-9.22, -9.84) * mm, "end": v(10, -9.84) * mm});
            skSolve(sketch);
        }
        {
            var Q0;
            Q0=sQuery(id+"F6.wireOp",EDGE,"E295.MirrorCS");
            var Q1;
            Q1=sQuery(id+"F6.wireOp",VERTEX,"E274.MirrorCS.end");
            cPlane(context, id + "F7", {"entities" : qUnion([Q0, Q1]), "cplaneType" : CPlaneType.LINE_POINT, "offset" : 25 * mm, "width" : 150 * mm, "height" : 150 * mm});
        }
        {
            var Q0;
            Q0=qCreatedBy(id+"F7.planeOp",FACE);
            var sketch = newSketch(context, id + "F8", { "sketchPlane" : qUnion([Q0])});
            skCircle(sketch, "E362", {"center": v(9.84, 0.62) * mm, "radius": 0.2 * mm});
            skSolve(sketch);
        }
        {
            var Q0;
            Q0=makeQuery(id+"F8.imprint","IMPRINT",FACE,{"disambiguationData":[TD([[makeQuery(id+"F8.imprint","IMPRINT",EDGE,{"derivedFrom":sQuery(id+"F8.wireOp",EDGE,"E362")}),1.0]])]});
            var Q1;
            Q1=sQuery(id+"F6.wireOp",EDGE,"E295.MirrorCS");
            var Q2;
            Q2=sQuery(id+"F6.wireOp",EDGE,"E344.MirrorCS");
            var Q3;
            Q3=sQuery(id+"F6.wireOp",EDGE,"E350.MirrorCS");
            var Q4;
            Q4=sQuery(id+"F6.wireOp",EDGE,"E331.MirrorCS");
            var Q5;
            Q5=sQuery(id+"F6.wireOp",EDGE,"E356.MirrorCS");
            var Q6;
            Q6=sQuery(id+"F6.wireOp",EDGE,"E336.MirrorCS");
            var Q7;
            Q7=sQuery(id+"F6.wireOp",EDGE,"E275.MirrorCS");
            var Q8;
            Q8=sQuery(id+"F6.wireOp",EDGE,"E303.MirrorCS");
            var Q9;
            Q9=sQuery(id+"F6.wireOp",EDGE,"E268.MirrorCS");
            var Q10;
            Q10=sQuery(id+"F6.wireOp",EDGE,"E301.MirrorCS");
            var Q11;
            Q11=sQuery(id+"F6.wireOp",EDGE,"E286.MirrorCS");
            var Q12;
            Q12=sQuery(id+"F6.wireOp",EDGE,"E313.MirrorCS");
            var Q13;
            Q13=sQuery(id+"F6.wireOp",EDGE,"E287.MirrorCS");
            var Q14;
            Q14=sQuery(id+"F6.wireOp",EDGE,"E327.MirrorCS");
            var Q15;
            Q15=sQuery(id+"F6.wireOp",EDGE,"E262.MirrorCS");
            var Q16;
            Q16=sQuery(id+"F6.wireOp",EDGE,"E260.MirrorCS");
            var Q17;
            Q17=sQuery(id+"F6.wireOp",EDGE,"E320.MirrorCS");
            var Q18;
            Q18=sQuery(id+"F6.wireOp",EDGE,"E298.MirrorCS");
            var Q19;
            Q19=sQuery(id+"F6.wireOp",EDGE,"E276.MirrorCS");
            var Q20;
            Q20=sQuery(id+"F6.wireOp",EDGE,"E354.MirrorCS");
            var Q21;
            Q21=sQuery(id+"F6.wireOp",EDGE,"E340.MirrorCS");
            var Q22;
            Q22=sQuery(id+"F6.wireOp",EDGE,"E297.MirrorCS");
            var Q23;
            Q23=sQuery(id+"F6.wireOp",EDGE,"E314.MirrorCS");
            var Q24;
            Q24=sQuery(id+"F6.wireOp",EDGE,"E348.MirrorCS");
            var Q25;
            Q25=sQuery(id+"F6.wireOp",EDGE,"E359.MirrorCS");
            var Q26;
            Q26=sQuery(id+"F6.wireOp",EDGE,"E322.MirrorCS");
            var Q27;
            Q27=sQuery(id+"F6.wireOp",EDGE,"E308.MirrorCS");
            var Q28;
            Q28=sQuery(id+"F6.wireOp",EDGE,"E292.MirrorCS");
            var Q29;
            Q29=sQuery(id+"F6.wireOp",EDGE,"E328.MirrorCS");
            var Q30;
            Q30=sQuery(id+"F6.wireOp",EDGE,"E333.MirrorCS");
            var Q31;
            Q31=sQuery(id+"F6.wireOp",EDGE,"E293.MirrorCS");
            var Q32;
            Q32=sQuery(id+"F6.wireOp",EDGE,"E353.MirrorCS");
            var Q33;
            Q33=sQuery(id+"F6.wireOp",EDGE,"E361");
            sweep(context, id + "F9", {"profiles" : qUnion([Q0]), "path" : qUnion([Q1, Q2, Q3, Q4, Q5, Q6, Q7, Q8, Q9, Q10, Q11, Q12, Q13, Q14, Q15, Q16, Q17, Q18, Q19, Q20, Q21, Q22, Q23, Q24, Q25, Q26, Q27, Q28, Q29, Q30, Q31, Q32, Q33])});
        }
    });
